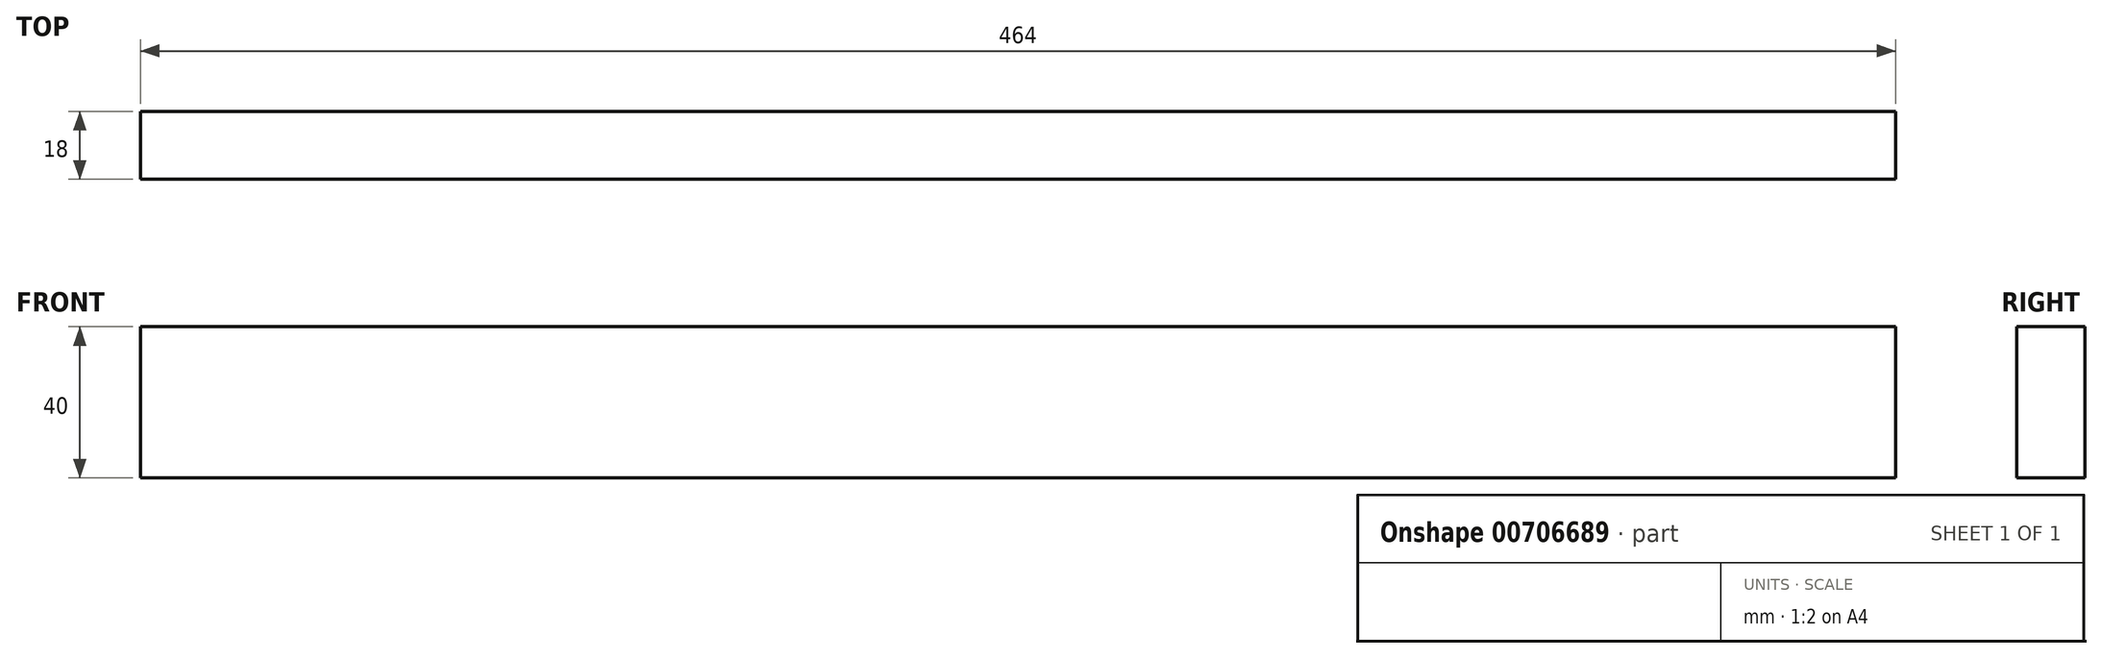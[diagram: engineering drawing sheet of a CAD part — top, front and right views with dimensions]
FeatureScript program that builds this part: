
annotation { "Feature Type Name" : "Feature", "Feature Type Description" : "" }
export const myFeature = defineFeature(function(context is Context, id is Id, definition is map)
    precondition{}
    {
        {
            var Q0;
            Q0=qCreatedBy(makeId("Front.planeOp"),FACE);
            var sketch = newSketch(context, id + "F0", { "sketchPlane" : qUnion([Q0])});
            skLineSegment(sketch, "E0.bottom", {"start": v(-232, -20) * mm, "end": v(232, -20) * mm});
            skLineSegment(sketch, "E0.top", {"start": v(-232, 20) * mm, "end": v(232, 20) * mm});
            skLineSegment(sketch, "E0.left", {"start": v(-232, -20) * mm, "end": v(-232, 20) * mm});
            skLineSegment(sketch, "E0.right", {"start": v(232, -20) * mm, "end": v(232, 20) * mm});
            skPoint(sketch, "E0.middle", {"position": v(0, 0) * mm});
            skSolve(sketch);
        }
        {
            var Q0;
            Q0=makeQuery(id+"F0.imprint","IMPRINT",FACE,{"disambiguationData":[TD([[makeQuery(id+"F0.imprint","IMPRINT",EDGE,{"derivedFrom":sQuery(id+"F0.wireOp",EDGE,"E0.bottom")}),1.0]])]});
            extrude(context, id + "F1", {"entities" : qUnion([Q0]), "depth" : 18 * mm, "offsetDistance" : 25 * mm, "symmetric" : true});
        }
    });
